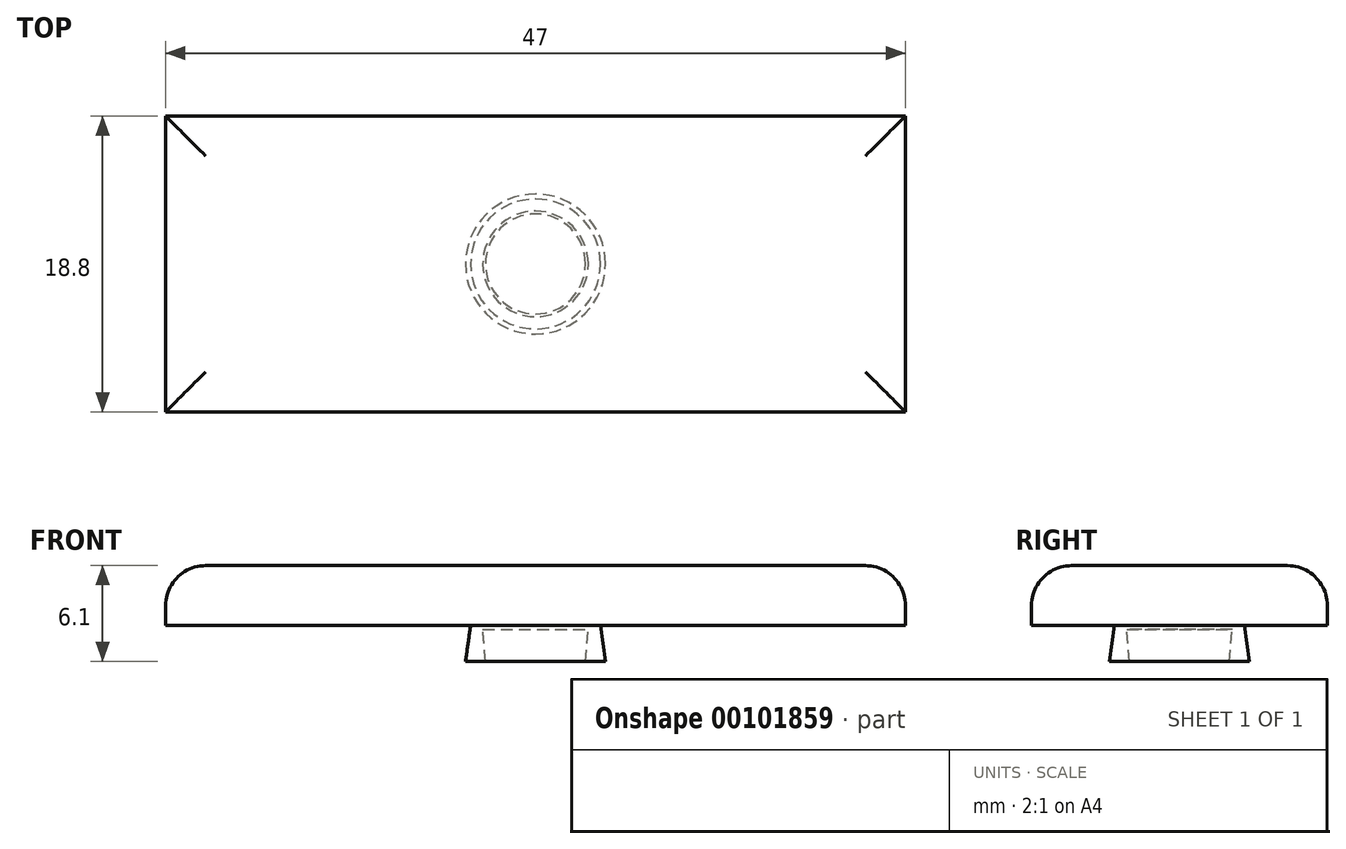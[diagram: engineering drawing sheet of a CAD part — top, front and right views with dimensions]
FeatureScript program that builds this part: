
annotation { "Feature Type Name" : "Feature", "Feature Type Description" : "" }
export const myFeature = defineFeature(function(context is Context, id is Id, definition is map)
    precondition{}
    {
        {
            var Q0;
            Q0=qCreatedBy(makeId("Top.planeOp"),FACE);
            var sketch = newSketch(context, id + "F0", { "sketchPlane" : qUnion([Q0])});
            skLineSegment(sketch, "E0.bottom", {"start": v(23.5, 9.4) * mm, "end": v(-23.5, 9.4) * mm});
            skLineSegment(sketch, "E0.top", {"start": v(23.5, -9.4) * mm, "end": v(-23.5, -9.4) * mm});
            skLineSegment(sketch, "E0.left", {"start": v(23.5, 9.4) * mm, "end": v(23.5, -9.4) * mm});
            skLineSegment(sketch, "E0.right", {"start": v(-23.5, 9.4) * mm, "end": v(-23.5, -9.4) * mm});
            skPoint(sketch, "E0.middle", {"position": v(0, 0) * mm});
            skSolve(sketch);
        }
        {
            var Q0;
            Q0=makeQuery(id+"F0.imprint","IMPRINT",FACE,{"disambiguationData":[TD([[makeQuery(id+"F0.imprint","IMPRINT",EDGE,{"derivedFrom":sQuery(id+"F0.wireOp",EDGE,"E0.bottom")}),1.0]])]});
            extrude(context, id + "F1", {"entities" : qUnion([Q0]), "depth" : 6.1 * mm});
        }
        {
            var Q0;
            Q0=makeQuery(id+"F1.opExtrude","CAP_EDGE",EDGE,{"disambiguationData":[OSD([sQuery(id+"F0.wireOp",EDGE,"E0.right")])],"isStart":false});
            var Q1;
            Q1=makeQuery(id+"F1.opExtrude","CAP_EDGE",EDGE,{"disambiguationData":[OSD([sQuery(id+"F0.wireOp",EDGE,"E0.left")])],"isStart":false});
            var Q2;
            Q2=makeQuery(id+"F1.opExtrude","CAP_EDGE",EDGE,{"disambiguationData":[OSD([sQuery(id+"F0.wireOp",EDGE,"E0.top")])],"isStart":false});
            var Q3;
            Q3=makeQuery(id+"F1.opExtrude","CAP_EDGE",EDGE,{"disambiguationData":[OSD([sQuery(id+"F0.wireOp",EDGE,"E0.bottom")])],"isStart":false});
            fillet(context, id + "F2", {"entities" : qUnion([Q0, Q1, Q2, Q3]), "radius" : 2.54 * mm, "tangentPropagation" : true, "allowEdgeOverflow" : false});
        }
        {
            var Q0;
            Q0=makeQuery(id+"F1.opExtrude","CAP_FACE",FACE,{"disambiguationData":[OSD([sQuery(id+"F0.wireOp",EDGE,"E0.bottom"),sQuery(id+"F0.wireOp",EDGE,"E0.top"),sQuery(id+"F0.wireOp",EDGE,"E0.left"),sQuery(id+"F0.wireOp",EDGE,"E0.right")])],"isStart":true});
            var sketch = newSketch(context, id + "F3", { "sketchPlane" : qUnion([Q0])});
            skCircle(sketch, "E1", {"center": v(0, 0) * mm, "radius": 4.45 * mm});
            skLineSegment(sketch, "E2.bottom", {"start": v(-23.5, 9.4) * mm, "end": v(23.5, 9.4) * mm});
            skLineSegment(sketch, "E2.top", {"start": v(-23.5, -9.4) * mm, "end": v(23.5, -9.4) * mm});
            skLineSegment(sketch, "E2.left", {"start": v(-23.5, 9.4) * mm, "end": v(-23.5, -9.4) * mm});
            skLineSegment(sketch, "E2.right", {"start": v(23.5, 9.4) * mm, "end": v(23.5, -9.4) * mm});
            skSolve(sketch);
        }
        {
            var Q0;
            Q0=makeQuery(id+"F3.imprint","IMPRINT",FACE,{"disambiguationData":[TD([[makeQuery(id+"F3.imprint","IMPRINT",EDGE,{"derivedFrom":sQuery(id+"F3.wireOp",EDGE,"E1")}),-1.0]])]});
            extrude(context, id + "F4", {"entities" : qUnion([Q0]), "operationType" : NewBodyOperationType.REMOVE, "oppositeDirection" : true, "depth" : 3.56 * mm, "hasDraft" : true, "draftAngle" : 8 * degree});
        }
        {
            var Q0;
            Q0=makeQuery(id+"F1.opExtrude","CAP_FACE",FACE,{"disambiguationData":[OSD([sQuery(id+"F0.wireOp",EDGE,"E0.bottom"),sQuery(id+"F0.wireOp",EDGE,"E0.top"),sQuery(id+"F0.wireOp",EDGE,"E0.left"),sQuery(id+"F0.wireOp",EDGE,"E0.right")])],"isStart":true});
            var sketch = newSketch(context, id + "F5", { "sketchPlane" : qUnion([Q0])});
            skCircle(sketch, "E3", {"center": v(0, 0) * mm, "radius": 3.18 * mm});
            skSolve(sketch);
        }
        {
            var Q0;
            Q0=makeQuery(id+"F5.imprint","IMPRINT",FACE,{"disambiguationData":[TD([[makeQuery(id+"F5.imprint","IMPRINT",EDGE,{"derivedFrom":sQuery(id+"F5.wireOp",EDGE,"E3")}),1.0]])]});
            extrude(context, id + "F6", {"entities" : qUnion([Q0]), "operationType" : NewBodyOperationType.REMOVE, "oppositeDirection" : true, "depth" : 2.03 * mm, "hasDraft" : true, "draftAngle" : 5 * degree});
        }
        {
            var Q0;
            Q0=makeQuery(id+"F4.boolean.opBoolean","COPY",FACE,{"derivedFrom":makeQuery(id+"F4.opExtrude","CAP_FACE",FACE,{"disambiguationData":[OSD([sQuery(id+"F3.wireOp",EDGE,"E1"),sQuery(id+"F3.wireOp",EDGE,"E2.bottom"),sQuery(id+"F3.wireOp",EDGE,"E2.top"),sQuery(id+"F3.wireOp",EDGE,"E2.left"),sQuery(id+"F3.wireOp",EDGE,"E2.right")])],"isStart":false})});
            extrude(context, id + "F7", {"entities" : qUnion([Q0]), "operationType" : NewBodyOperationType.ADD, "depth" : 1.27 * mm});
        }
    });
